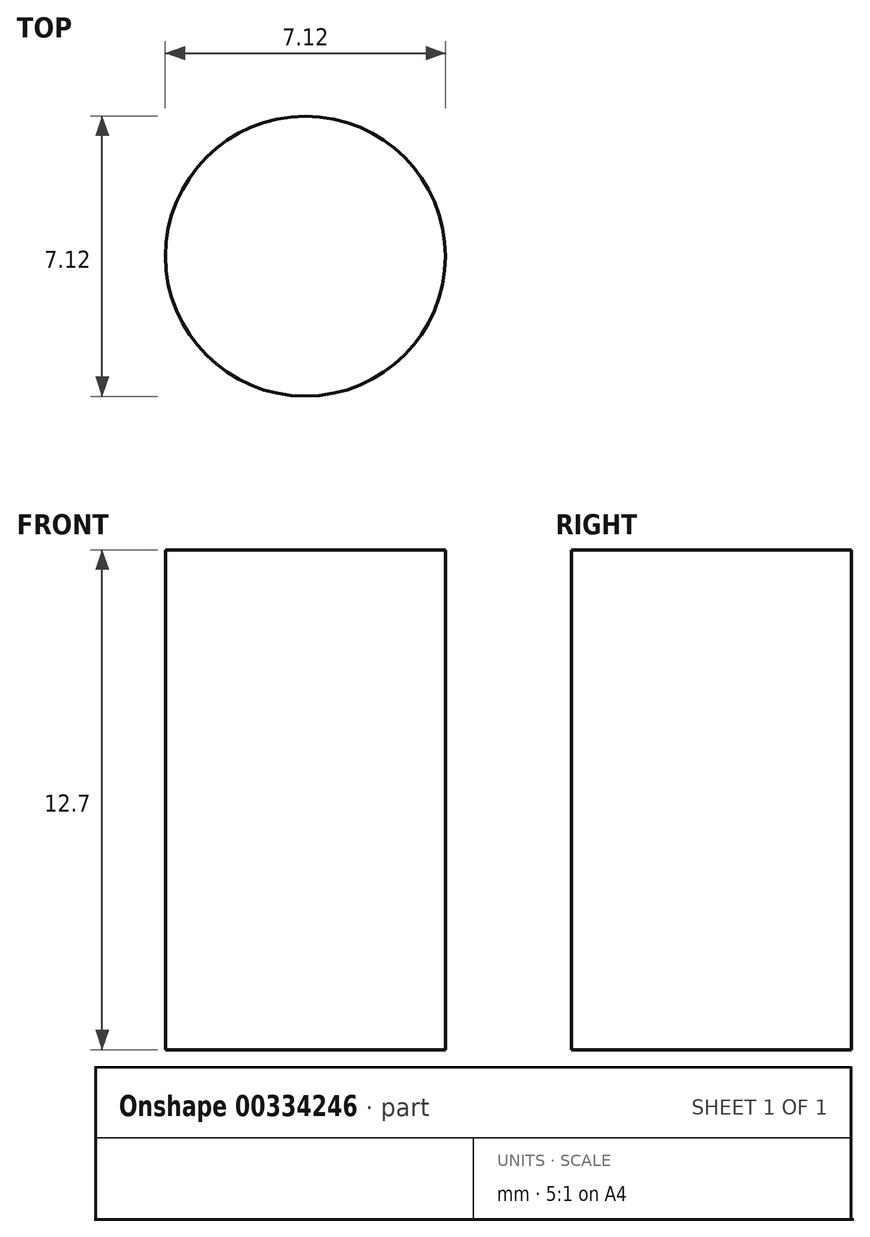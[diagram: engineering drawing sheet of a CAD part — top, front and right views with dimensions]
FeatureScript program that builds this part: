
annotation { "Feature Type Name" : "Feature", "Feature Type Description" : "" }
export const myFeature = defineFeature(function(context is Context, id is Id, definition is map)
    precondition{}
    {
        {
            var Q0;
            Q0=qCreatedBy(makeId("Top.planeOp"),FACE);
            var sketch = newSketch(context, id + "F0", { "sketchPlane" : qUnion([Q0])});
            skCircle(sketch, "E0", {"center": v(0, 0) * mm, "radius": 3.56 * mm});
            skSolve(sketch);
        }
        {
            var Q0;
            Q0=makeQuery(id+"F0.imprint","IMPRINT",FACE,{"disambiguationData":[TD([[makeQuery(id+"F0.imprint","IMPRINT",EDGE,{"derivedFrom":sQuery(id+"F0.wireOp",EDGE,"E0")}),1.0]])]});
            extrude(context, id + "F1", {"entities" : qUnion([Q0]), "depth" : 12.7 * mm});
        }
    });
